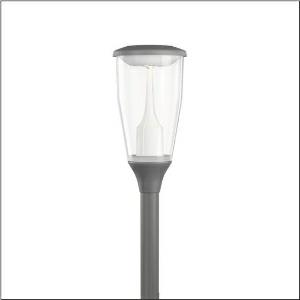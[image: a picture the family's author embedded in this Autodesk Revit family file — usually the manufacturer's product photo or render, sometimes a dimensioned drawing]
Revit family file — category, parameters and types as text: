
# Revit family: dl_11_iq___st1_2a_5xa5575mf14h000022_93a8
name_source: partatom
category: Lighting Fixtures
units: mm (PartAtom-declared; Revit-internal decimal feet)

## family parameters
Cut with Voids When Loaded = No
Host = Face
Light Source = No
Part Type = Normal
Room Calculation Point = No
Round Connector Dimension = Use Diameter
Shared = No

## types (1)
- --- (1 x LED, 1560 lm, 11.8 W, 2700K)
    Apparent Load = 12 VA
    CIE Flux Codes = 24 63 94 96 100
    Color Rendering = 70
    Color Temperature = 2700K
    Default Elevation = 1800 mm
    Description = DL 11 iQ, mast luminaire, Module 540 iQ-SR, primary light control with 3 zone facetted reflector, of plastic, silver coated, highly specular, structured, primary optical cover: cover, of PMMA, transparent, light distribution: ST1.2a, light emission: direct distribution, primary light characteristic: asymmetric, installation type: post-top, LED, High Power LED, rated luminous flux: 1.560lm, luminous efficacy: 149lm/W, light colour: 727, colour temperature: 2700K, control gear: iQ Street-Remote, control: Street-Remote, Auto-Match, Temp-Guard, Lumen-Switch, Night-Set, Smart-Wire, Light-Fading, Desk-Remote (wireless, voltage-free reading and setting of iQ features in the workshop via application-optimized NFC function/RFID function), optimised constant luminous flux control (CLO 2.0), mains connection: 220..240V, AC, 50/60Hz, connection cable pre-assembled, cable length: 5,5m, wiring characteristics: H07RN-F, 5-core, 1.5mm², start of lifetime: 12W, end of service life: 12W, reduction: 5W, luminaire housing, upper part, of diecast aluminium, coated, Siteco® metallic grey (DB 702S), spigot size: 76mm (post-top), mounting height: 3..5m, post-top mast mounting element, of diecast aluminium, coated, Siteco® metallic grey (DB 702S), Module 540 iQ-SR, traffic white (RAL 9016), equipment: standard, protection rating (complete): IP66, insulation class (complete): insulation class II (safety insulation), certification: CE, ENEC, ENEC+, VDE, impact resistance: IK07, packaging unit: 1 piece

Light Distribution: ST1.2a
    Height = 665 mm
    Lamp = 1 x LED
    Lamp Light Flux = 1560 lm
    Lamp Power = 11.8 W
    Lamp count = 1
    Length = 334 mm
    Luminous efficacy = 132 lm/W
    Manufacturer = Siteco
    ModVariant = No
    Model = 5XA5575MF14H000022
    Number of Poles = 1
    OnlyDefault = Yes
    Power Factor = 1
    Product Name = DL 11 iQ | ST1.2a
    Product group = mast luminaire | pylon top
    ProductGroupID = 6100
    Protection Class = Protection class II
    Protection Degree = IP 66
    RLX_Detail_Level = 1
    RLX_Emergency_Light_Flux = 0 lm
    RLX_Emergency_Type = 0
    RLX_Emergency_Type_DB = No
    RlxData = <blob elided: 152805 chars, md5=ea3dffca>
    Socket = socket
    Standby Power = 0 W
    System Light Flux = 1560 lm
    System Power = 12 W
    Type Comments = factory setting: luminous flux: 100 % | dim-lin: 254 | 472 mA
    Type Image = l_1258354.jpg
    URL = http://relux.com
    VarID = @adj_094832
    Voltage = 0 V
    Weight = 0.00 kg
    Width = 0 mm  [stored 0 ft]

note: [stored X ft] marks values corroborated as IEEE doubles in the binary element streams (Revit-internal decimal feet)

## geometry (parser evidence)
native form markers: Blend x4, Sweep x11
no freeform markers — native parametric forms only
